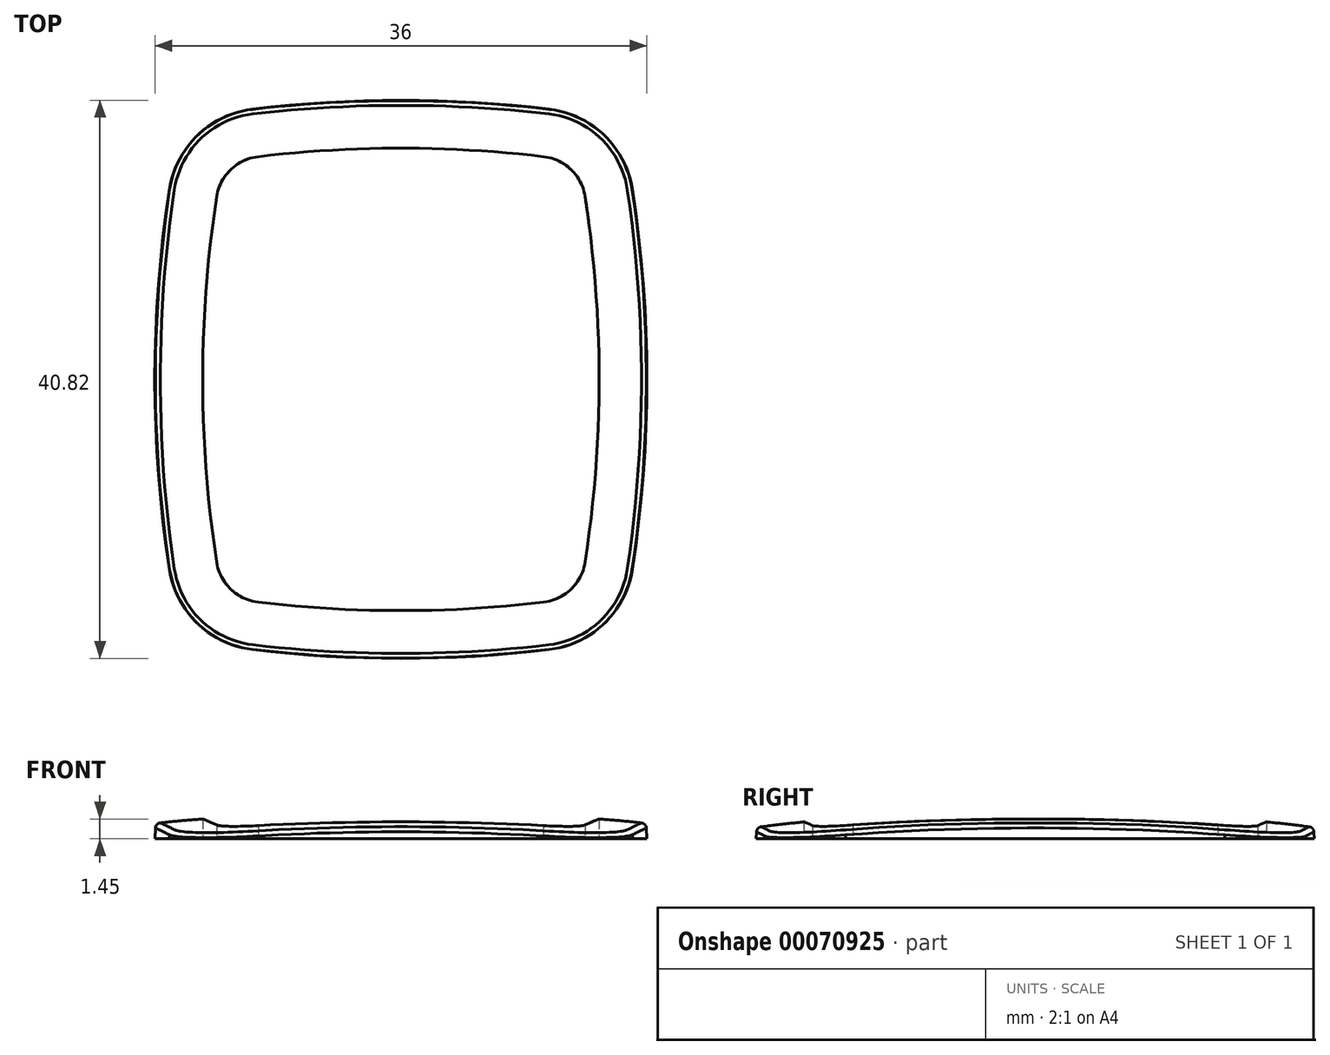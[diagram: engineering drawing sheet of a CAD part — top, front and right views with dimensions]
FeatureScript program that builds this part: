
annotation { "Feature Type Name" : "Feature", "Feature Type Description" : "" }
export const myFeature = defineFeature(function(context is Context, id is Id, definition is map)
    precondition{}
    {
        {
            var Q0;
            Q0=qCreatedBy(makeId("Top.planeOp"),FACE);
            var sketch = newSketch(context, id + "F0", { "sketchPlane" : qUnion([Q0])});
            skLineSegment(sketch, "E0.bottom", {"start": v(12, -12) * mm, "end": v(-12, -12) * mm, "construction": true});
            skLineSegment(sketch, "E0.top", {"start": v(12, 12) * mm, "end": v(-12, 12) * mm, "construction": true});
            skLineSegment(sketch, "E0.left", {"start": v(12, -12) * mm, "end": v(12, 12) * mm, "construction": true});
            skLineSegment(sketch, "E0.right", {"start": v(-12, -12) * mm, "end": v(-12, 12) * mm, "construction": true});
            skPoint(sketch, "E0.middle", {"position": v(0, 0) * mm});
            skLineSegment(sketch, "E1.bottom", {"start": v(-16, 19) * mm, "end": v(16, 19) * mm, "construction": true});
            skLineSegment(sketch, "E1.top", {"start": v(-16, -19) * mm, "end": v(16, -19) * mm, "construction": true});
            skLineSegment(sketch, "E1.left", {"start": v(-16, 19) * mm, "end": v(-16, -19) * mm, "construction": true});
            skLineSegment(sketch, "E1.right", {"start": v(16, 19) * mm, "end": v(16, -19) * mm, "construction": true});
            skArc(sketch, "E2", {"start": v(-16, 19) * mm, "mid": v(-18, 0) * mm, "end": v(-16, -19) * mm});
            skArc(sketch, "E3", {"start": v(16, 19) * mm, "mid": v(0, 20.41) * mm, "end": v(-16, 19) * mm});
            skArc(sketch, "E4", {"start": v(16, -19) * mm, "mid": v(18, 0) * mm, "end": v(16, 19) * mm});
            skArc(sketch, "E5", {"start": v(-16, -19) * mm, "mid": v(0, -20.41) * mm, "end": v(16, -19) * mm});
            skSolve(sketch);
        }
        {
            var Q0;
            Q0 = qSketchRegion(id + "F0", true);
            extrude(context, id + "F1", {"entities" : qUnion([Q0]), "depth" : 1.5 * mm, "hasDraft" : true, "draftAngle" : 3 * degree, "draftPullDirection" : true});
        }
        {
            var Q0;
            Q0=makeQuery(id+"F1.opExtrude","SWEPT_EDGE",EDGE,{"disambiguationData":[OSD([sQuery(id+"F0.wireOp",EDGE,"E2"),sQuery(id+"F0.wireOp",EDGE,"E5")])]});
            var Q1;
            Q1=makeQuery(id+"F1.opExtrude","SWEPT_EDGE",EDGE,{"disambiguationData":[OSD([sQuery(id+"F0.wireOp",EDGE,"E4"),sQuery(id+"F0.wireOp",EDGE,"E5")])]});
            var Q2;
            Q2=makeQuery(id+"F1.opExtrude","SWEPT_EDGE",EDGE,{"disambiguationData":[OSD([sQuery(id+"F0.wireOp",EDGE,"E3"),sQuery(id+"F0.wireOp",EDGE,"E4")])]});
            var Q3;
            Q3=makeQuery(id+"F1.opExtrude","SWEPT_EDGE",EDGE,{"disambiguationData":[OSD([sQuery(id+"F0.wireOp",EDGE,"E2"),sQuery(id+"F0.wireOp",EDGE,"E3")])]});
            fillet(context, id + "F2", {"entities" : qUnion([Q0, Q1, Q2, Q3]), "radius" : 7 * mm, "tangentPropagation" : true, "allowEdgeOverflow" : false});
        }
        {
            var Q0;
            Q0=qCreatedBy(makeId("Front.planeOp"),FACE);
            var sketch = newSketch(context, id + "F3", { "sketchPlane" : qUnion([Q0])});
            skArc(sketch, "E6", {"start": v(0, 1.5) * mm, "mid": v(-14.07, 1.48) * mm, "end": v(-28, -0.5) * mm});
            skPoint(sketch, "E7.orphan", {"position": v(0, 8) * mm});
            skLineSegment(sketch, "E8", {"start": v(-28, -0.5) * mm, "end": v(-28, 2.5) * mm});
            skLineSegment(sketch, "E9", {"start": v(0, 1.5) * mm, "end": v(0, 15.49) * mm, "construction": true});
            skLineSegment(sketch, "E10", {"start": v(0, 1.5) * mm, "end": v(0, 2.5) * mm});
            skLineSegment(sketch, "E11", {"start": v(0, 2.5) * mm, "end": v(-28, 2.5) * mm});
            skSolve(sketch);
        }
        {
            var Q0;
            Q0 = qSketchRegion(id + "F3", true);
            var Q1;
            Q1=sQuery(id+"F3.wireOp",EDGE,"E9");
            revolve(context, id + "F4", {"operationType" : NewBodyOperationType.REMOVE, "entities" : qUnion([Q0]), "axis" : qUnion([Q1]), "revolveType" : RevolveType.FULL, "oppositeDirection" : true});
        }
        {
            var Q0;
            Q0=qCreatedBy(makeId("Top.planeOp"),FACE);
            var sketch = newSketch(context, id + "F5", { "sketchPlane" : qUnion([Q0])});
            skFitSpline(sketch, "E12.0", {"points": [v(10.44, 16.3) * mm, v(10.63, 16.27) * mm, v(11, 16.2) * mm, v(11.44, 16.03) * mm, v(11.78, 15.85) * mm, v(12.02, 15.7) * mm, v(12.24, 15.53) * mm, v(12.45, 15.34) * mm, v(12.65, 15.13) * mm, v(12.83, 14.91) * mm, v(12.99, 14.68) * mm, v(13.13, 14.44) * mm, v(13.25, 14.17) * mm, v(13.38, 13.82) * mm, v(13.45, 13.55) * mm, v(13.48, 13.36) * mm]});
            skArc(sketch, "E12.1", {"start": v(13.48, -13.36) * mm, "mid": v(14.5, 0) * mm, "end": v(13.48, 13.36) * mm});
            skArc(sketch, "E12.2", {"start": v(10.44, 16.3) * mm, "mid": v(0, 16.91) * mm, "end": v(-10.44, 16.3) * mm});
            skFitSpline(sketch, "E12.3", {"points": [v(13.48, -13.36) * mm, v(13.45, -13.55) * mm, v(13.36, -13.91) * mm, v(13.18, -14.35) * mm, v(12.99, -14.68) * mm, v(12.83, -14.91) * mm, v(12.65, -15.13) * mm, v(12.46, -15.33) * mm, v(12.24, -15.53) * mm, v(12.02, -15.7) * mm, v(11.78, -15.85) * mm, v(11.53, -15.98) * mm, v(11.27, -16.1) * mm, v(10.91, -16.21) * mm, v(10.63, -16.27) * mm, v(10.44, -16.3) * mm]});
            skFitSpline(sketch, "E12.4", {"points": [v(-13.48, 13.36) * mm, v(-13.45, 13.55) * mm, v(-13.36, 13.91) * mm, v(-13.18, 14.35) * mm, v(-12.99, 14.68) * mm, v(-12.83, 14.91) * mm, v(-12.65, 15.13) * mm, v(-12.46, 15.33) * mm, v(-12.24, 15.53) * mm, v(-12.02, 15.7) * mm, v(-11.78, 15.85) * mm, v(-11.53, 15.98) * mm, v(-11.27, 16.1) * mm, v(-10.91, 16.21) * mm, v(-10.63, 16.27) * mm, v(-10.44, 16.3) * mm]});
            skArc(sketch, "E12.5", {"start": v(-13.48, 13.36) * mm, "mid": v(-14.5, 0) * mm, "end": v(-13.48, -13.36) * mm});
            skFitSpline(sketch, "E12.6", {"points": [v(-10.44, -16.3) * mm, v(-10.63, -16.27) * mm, v(-11, -16.2) * mm, v(-11.44, -16.03) * mm, v(-11.78, -15.85) * mm, v(-12.02, -15.7) * mm, v(-12.24, -15.53) * mm, v(-12.45, -15.34) * mm, v(-12.65, -15.13) * mm, v(-12.83, -14.91) * mm, v(-12.99, -14.68) * mm, v(-13.13, -14.44) * mm, v(-13.25, -14.17) * mm, v(-13.38, -13.82) * mm, v(-13.45, -13.55) * mm, v(-13.48, -13.36) * mm]});
            skArc(sketch, "E12.7", {"start": v(-10.44, -16.3) * mm, "mid": v(0, -16.91) * mm, "end": v(10.44, -16.3) * mm});
            skSolve(sketch);
        }
        {
            var Q0;
            Q0=makeQuery(id+"F4.boolean.opBoolean","INTERSECT",EDGE,{"derivedFrom":[makeQuery(id+"F2.opFillet","BLEND_FACE",FACE,{"disambiguationData":[OSD([sQuery(id+"F0.wireOp",EDGE,"E2"),sQuery(id+"F0.wireOp",EDGE,"E3")])]}),makeQuery(id+"F4.opRevolve","SWEPT_FACE",FACE,{"disambiguationData":[OSD([sQuery(id+"F3.wireOp",EDGE,"E6")])]})]});
            fillet(context, id + "F6", {"entities" : qUnion([Q0]), "radius" : 0.4 * mm, "tangentPropagation" : true, "allowEdgeOverflow" : false});
        }
        {
            var Q0;
            Q0 = qSketchRegion(id + "F5", true);
            extrude(context, id + "F7", {"entities" : qUnion([Q0]), "operationType" : NewBodyOperationType.REMOVE, "endBound" : BoundingType.THROUGH_ALL, "depth" : 25 * mm});
        }
        {
            var Q0;
            Q0=qCreatedBy(makeId("Top.planeOp"),FACE);
            var sketch = newSketch(context, id + "F8", { "sketchPlane" : qUnion([Q0])});
            skLineSegment(sketch, "E13.bottom", {"start": v(13, 13) * mm, "end": v(-13, 13) * mm});
            skLineSegment(sketch, "E13.top", {"start": v(13, -13) * mm, "end": v(-13, -13) * mm});
            skLineSegment(sketch, "E13.left", {"start": v(13, 13) * mm, "end": v(13, -13) * mm});
            skLineSegment(sketch, "E13.right", {"start": v(-13, 13) * mm, "end": v(-13, -13) * mm});
            skPoint(sketch, "E13.middle", {"position": v(0, 0) * mm});
            skSolve(sketch);
        }
        {
            var Q0;
            Q0 = qSketchRegion(id + "F8", true);
            extrude(context, id + "F9", {"entities" : qUnion([Q0]), "operationType" : NewBodyOperationType.REMOVE, "depth" : 8.5 * mm});
        }
    });
